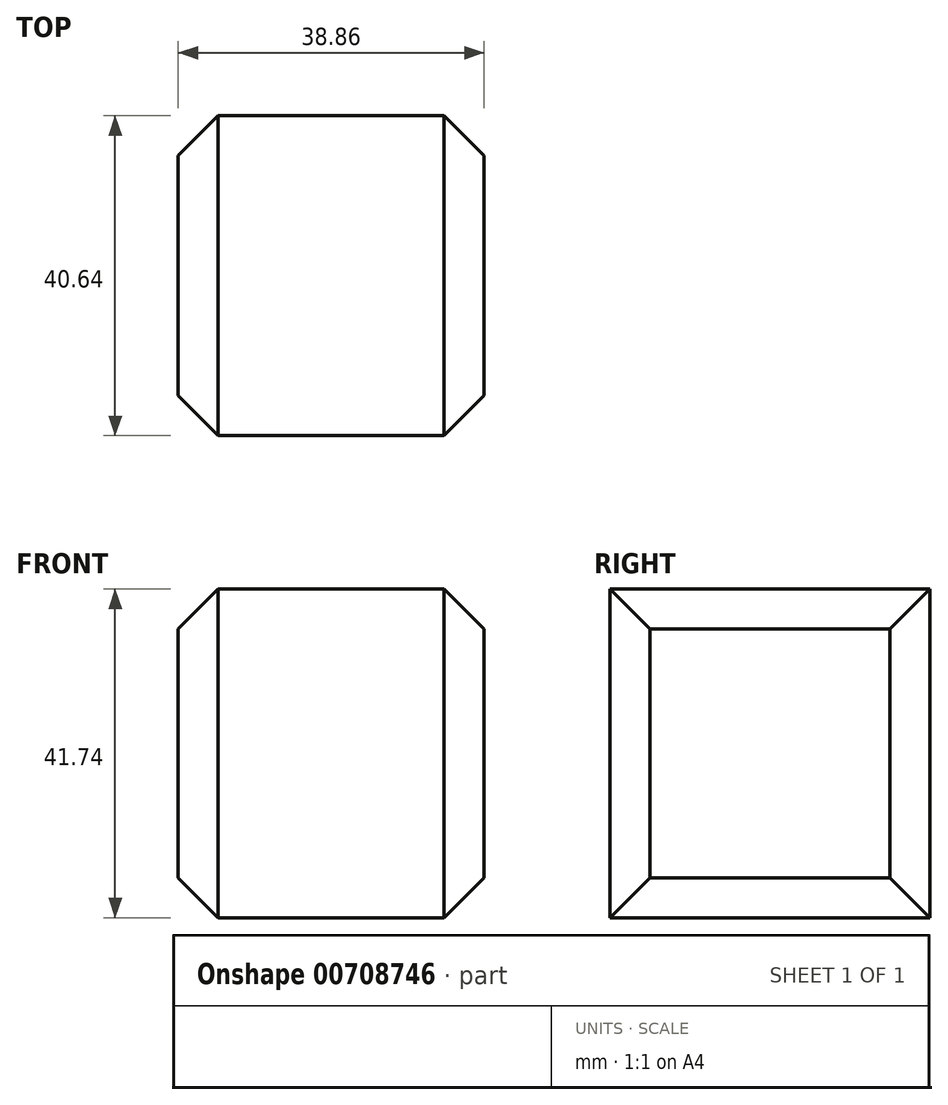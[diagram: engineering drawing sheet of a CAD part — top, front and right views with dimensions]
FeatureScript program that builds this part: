
annotation { "Feature Type Name" : "Feature", "Feature Type Description" : "" }
export const myFeature = defineFeature(function(context is Context, id is Id, definition is map)
    precondition{}
    {
        {
            var Q0;
            Q0=qCreatedBy(makeId("Front.planeOp"),FACE);
            var sketch = newSketch(context, id + "F0", { "sketchPlane" : qUnion([Q0])});
            skLineSegment(sketch, "E0.bottom", {"start": v(19.43, 20.87) * mm, "end": v(-19.43, 20.87) * mm});
            skLineSegment(sketch, "E0.top", {"start": v(19.43, -20.87) * mm, "end": v(-19.43, -20.87) * mm});
            skLineSegment(sketch, "E0.left", {"start": v(19.43, 20.87) * mm, "end": v(19.43, -20.87) * mm});
            skLineSegment(sketch, "E0.right", {"start": v(-19.43, 20.87) * mm, "end": v(-19.43, -20.87) * mm});
            skPoint(sketch, "E0.middle", {"position": v(0, 0) * mm});
            skSolve(sketch);
        }
        {
            var Q0;
            Q0 = qSketchRegion(id + "F0", true);
            extrude(context, id + "F1", {"entities" : qUnion([Q0]), "depth" : 40.64 * mm, "offsetDistance" : 25.4 * mm});
        }
        {
            var Q0;
            Q0=makeQuery(id+"F1.opExtrude","SWEPT_FACE",FACE,{"disambiguationData":[OSD([sQuery(id+"F0.wireOp",EDGE,"E0.right")])]});
            chamfer(context, id + "F2", {"entities" : qUnion([Q0]), "width" : 5.08 * mm, "tangentPropagation" : true});
        }
        {
            var Q0;
            Q0=makeQuery(id+"F1.opExtrude","SWEPT_FACE",FACE,{"disambiguationData":[OSD([sQuery(id+"F0.wireOp",EDGE,"E0.left")])]});
            chamfer(context, id + "F3", {"entities" : qUnion([Q0]), "width" : 5.08 * mm, "tangentPropagation" : true});
        }
    });
